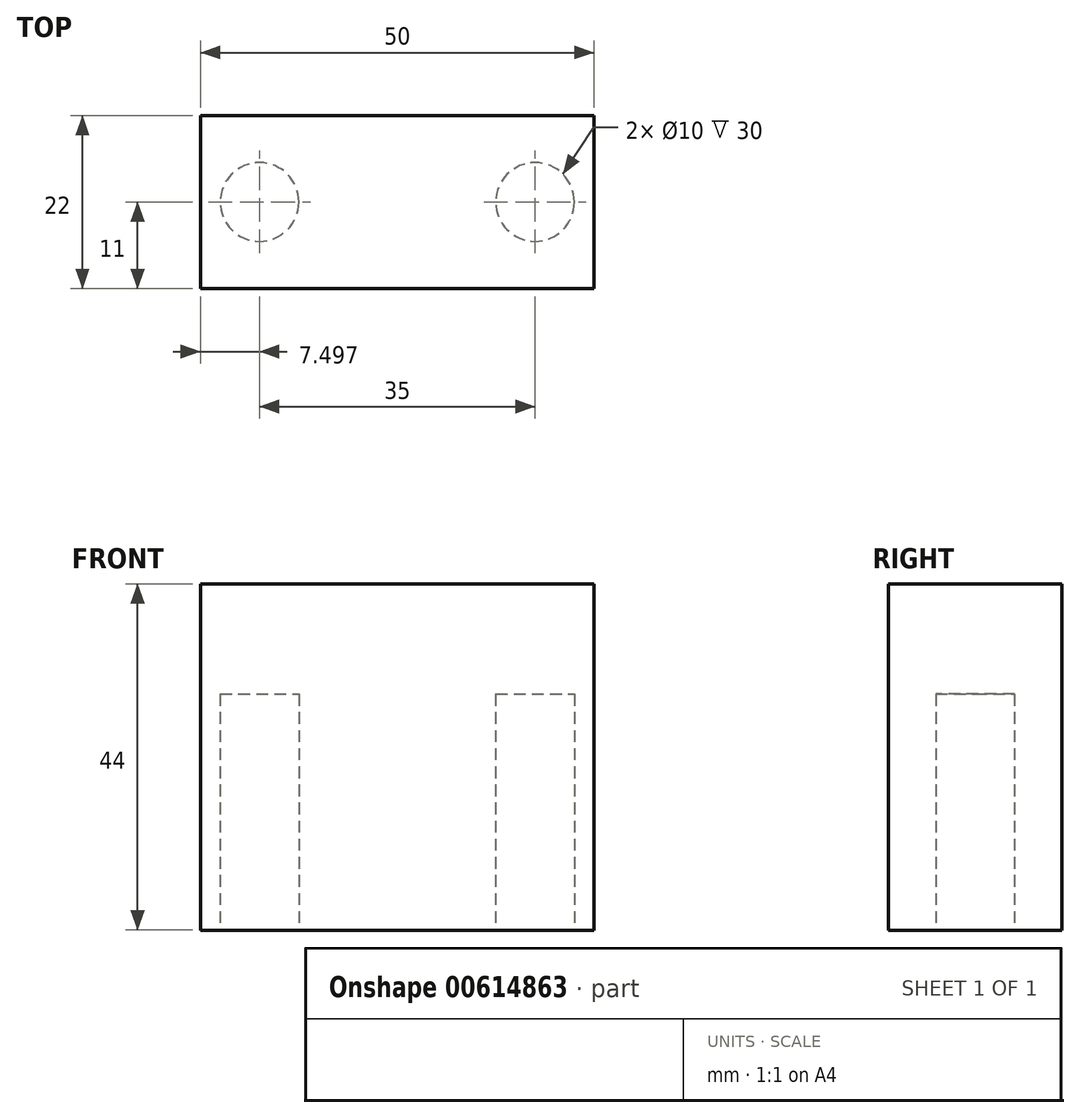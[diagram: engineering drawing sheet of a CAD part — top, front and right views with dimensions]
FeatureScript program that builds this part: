
annotation { "Feature Type Name" : "Feature", "Feature Type Description" : "" }
export const myFeature = defineFeature(function(context is Context, id is Id, definition is map)
    precondition{}
    {
        {
            var Q0;
            Q0=qCreatedBy(makeId("Front.planeOp"),FACE);
            cPlane(context, id + "F0", {"entities" : qUnion([Q0]), "cplaneType" : CPlaneType.OFFSET, "offset" : 25.4 * mm, "width" : 152.4 * mm, "height" : 152.4 * mm});
        }
        {
            var Q0;
            Q0=qCreatedBy(id+"F0.planeOp",FACE);
            var sketch = newSketch(context, id + "F1", { "sketchPlane" : qUnion([Q0])});
            skLineSegment(sketch, "E0.bottom", {"start": v(-14.75, 40.7) * mm, "end": v(35.25, 40.7) * mm});
            skLineSegment(sketch, "E0.top", {"start": v(-14.75, -3.3) * mm, "end": v(35.25, -3.3) * mm});
            skLineSegment(sketch, "E0.left", {"start": v(-14.75, 40.7) * mm, "end": v(-14.75, -3.3) * mm});
            skLineSegment(sketch, "E0.right", {"start": v(35.25, 40.7) * mm, "end": v(35.25, -3.3) * mm});
            skSolve(sketch);
        }
        {
            var Q0;
            Q0=makeQuery(id+"F1.imprint","IMPRINT",FACE,{"disambiguationData":[TD([[makeQuery(id+"F1.imprint","IMPRINT",EDGE,{"derivedFrom":sQuery(id+"F1.wireOp",EDGE,"E0.bottom")}),-1.0]])]});
            extrude(context, id + "F2", {"entities" : qUnion([Q0]), "depth" : 22 * mm, "offsetDistance" : 25.4 * mm});
        }
        {
            var Q0;
            Q0=makeQuery(id+"F2.opExtrude","SWEPT_FACE",FACE,{"disambiguationData":[OSD([sQuery(id+"F1.wireOp",EDGE,"E0.top")])]});
            var sketch = newSketch(context, id + "F3", { "sketchPlane" : qUnion([Q0])});
            skCircle(sketch, "E1", {"center": v(27.75, 36.4) * mm, "radius": 5 * mm});
            skCircle(sketch, "E2", {"center": v(-7.25, 36.4) * mm, "radius": 5 * mm});
            skSolve(sketch);
        }
        {
            var Q0;
            Q0 = qSketchRegion(id + "F3", true);
            extrude(context, id + "F4", {"entities" : qUnion([Q0]), "operationType" : NewBodyOperationType.REMOVE, "oppositeDirection" : true, "depth" : 30 * mm, "offsetDistance" : 25.4 * mm});
        }
    });
